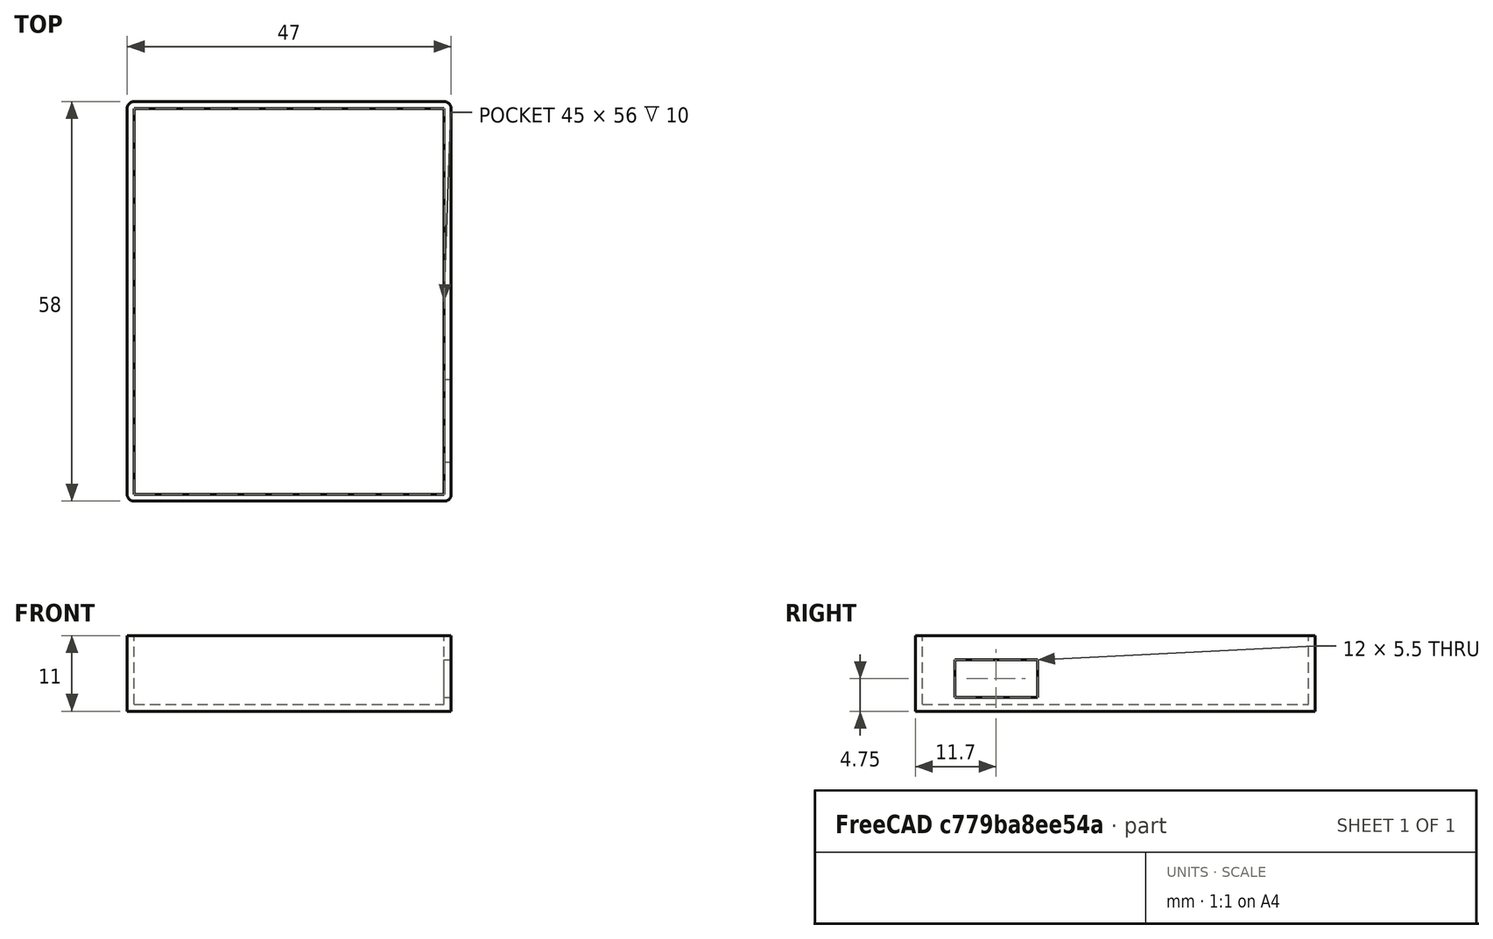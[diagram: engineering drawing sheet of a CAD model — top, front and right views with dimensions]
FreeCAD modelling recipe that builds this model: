
FCSTD DOCUMENT  (FreeCAD 0.18R16146 (Git))
Label: HR_v2
License: All rights reserved
LicenseURL: http://en.wikipedia.org/wiki/All_rights_reserved
objects: Part::Box×3, Part::Cut×2, Mesh::Feature×2, Part::Fillet×1
note: 6 computed .brp shape members not serialized (recipe doc carries the construction recipe); baked Part::Feature solids carry a one-line shape summary decoded from their .brp

FEATURE [Part::Box] Box  label="Cube"
  AttacherType = Attacher::AttachEngine3D
  Height = 11
  Length = 47
  Width = 58
FEATURE [Part::Box] Box001  label="Cube001"
  AttacherType = Attacher::AttachEngine3D
  Height = 10
  Length = 45
  Placement = pos=(1,1,1) rot=(0,0,1;0rad)
  Width = 56
FEATURE [Part::Cut] Cut
  Base = -> Box
  Refine = true
  Tool = -> Box001
FEATURE [Part::Fillet] Fillet
  Base = -> Cut
  Edges = 4 edges r=1: [Edge1,Edge3,Edge6,Edge15]
FEATURE [Mesh::Feature] parte_inferior
  Placement = pos=(1,56,-4) rot=(0,0,1;0rad)
FEATURE [Mesh::Feature] parte_inferior001
  Placement = pos=(1,0,-4) rot=(0,0,1;0rad)
FEATURE [Part::Box] Box002  label="Cube002"
  AttacherType = Attacher::AttachEngine3D
  Height = 5.5
  Length = 10
  Placement = pos=(41,5.7,2) rot=(0,0,1;0rad)
  Width = 12
FEATURE [Part::Cut] Cut001
  Base = -> Fillet
  Refine = true
  Tool = -> Box002
